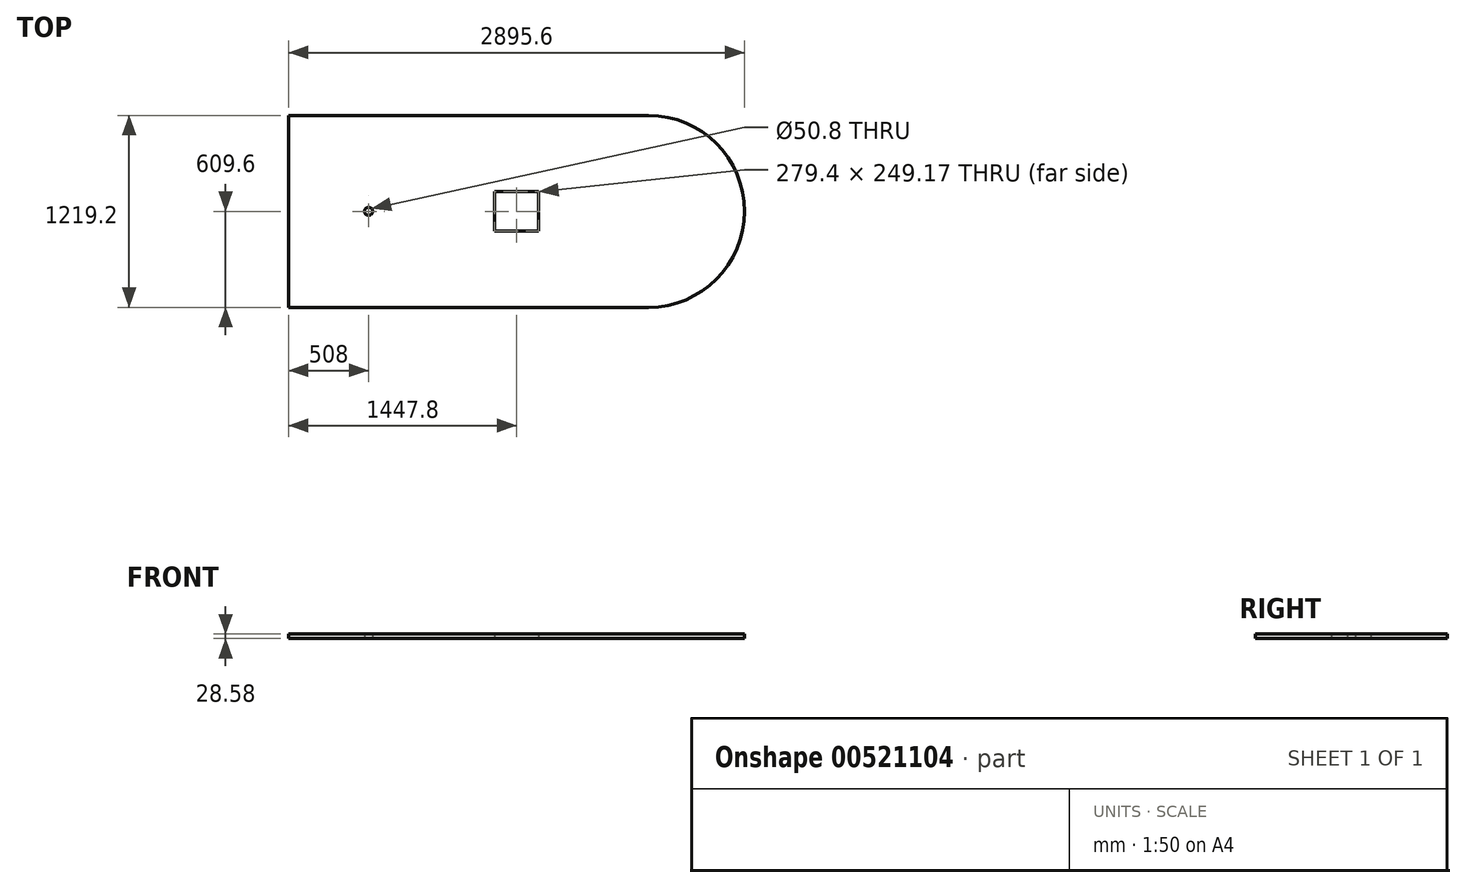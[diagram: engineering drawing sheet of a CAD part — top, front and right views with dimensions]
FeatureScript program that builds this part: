
annotation { "Feature Type Name" : "Feature", "Feature Type Description" : "" }
export const myFeature = defineFeature(function(context is Context, id is Id, definition is map)
    precondition{}
    {
        {
            var Q0;
            Q0=qCreatedBy(makeId("Top.planeOp"),FACE);
            var sketch = newSketch(context, id + "F0", { "sketchPlane" : qUnion([Q0])});
            skLineSegment(sketch, "E0.bottom", {"start": v(1447.8, 609.6) * mm, "end": v(-1371.6, 609.6) * mm});
            skLineSegment(sketch, "E0.top", {"start": v(1447.8, -609.6) * mm, "end": v(-1371.6, -609.6) * mm});
            skLineSegment(sketch, "E0.left", {"start": v(1447.8, 609.6) * mm, "end": v(1447.8, -609.6) * mm});
            skLineSegment(sketch, "E0.right", {"start": v(-1447.8, 533.4) * mm, "end": v(-1447.8, -533.4) * mm});
            skPoint(sketch, "E0.middle", {"position": v(0, 0) * mm});
            skPoint(sketch, "E1.endSnap0", {"position": v(1447.8, 0) * mm});
            skArc(sketch, "E2", {"start": v(838.2, 609.6) * mm, "mid": v(1447.8, 0) * mm, "end": v(838.2, -609.6) * mm});
            skPoint(sketch, "E3.visualSharp", {"position": v(-1447.8, 609.6) * mm});
            skPoint(sketch, "E4.visualSharp", {"position": v(-1447.8, -609.6) * mm});
            skLineSegment(sketch, "E5.bottom", {"start": v(139.7, 124.59) * mm, "end": v(-139.7, 124.59) * mm});
            skLineSegment(sketch, "E5.top", {"start": v(139.7, -124.59) * mm, "end": v(-139.7, -124.59) * mm});
            skLineSegment(sketch, "E5.left", {"start": v(139.7, 124.59) * mm, "end": v(139.7, -124.59) * mm});
            skLineSegment(sketch, "E5.right", {"start": v(-139.7, 124.59) * mm, "end": v(-139.7, -124.59) * mm});
            skLineSegment(sketch, "E6", {"start": v(-1447.8, 0) * mm, "end": v(-939.8, 0) * mm});
            skPoint(sketch, "E6.endSnap0", {"position": v(-1447.8, 0) * mm});
            skCircle(sketch, "E7", {"center": v(-939.8, 0) * mm, "radius": 25.4 * mm});
            skLineSegment(sketch, "E8", {"start": v(-1447.8, -533.4) * mm, "end": v(-1447.8, -609.6) * mm});
            skLineSegment(sketch, "E9", {"start": v(-1371.6, -609.6) * mm, "end": v(-1447.8, -609.6) * mm});
            skLineSegment(sketch, "E10", {"start": v(-1447.8, 533.4) * mm, "end": v(-1447.8, 609.6) * mm});
            skLineSegment(sketch, "E11", {"start": v(-1371.6, 609.6) * mm, "end": v(-1447.8, 609.6) * mm});
            skSolve(sketch);
        }
        {
            var Q0;
            Q0=makeQuery(id+"F0.imprint","IMPRINT",FACE,{"disambiguationData":[TD([[makeQuery(id+"F0.imprint","IMPRINT",EDGE,{"derivedFrom":sQuery(id+"F0.wireOp",EDGE,"E0.right")}),1.0]])]});
            extrude(context, id + "F1", {"entities" : qUnion([Q0]), "depth" : 28.57 * mm, "offsetDistance" : 25.4 * mm});
        }
    });
